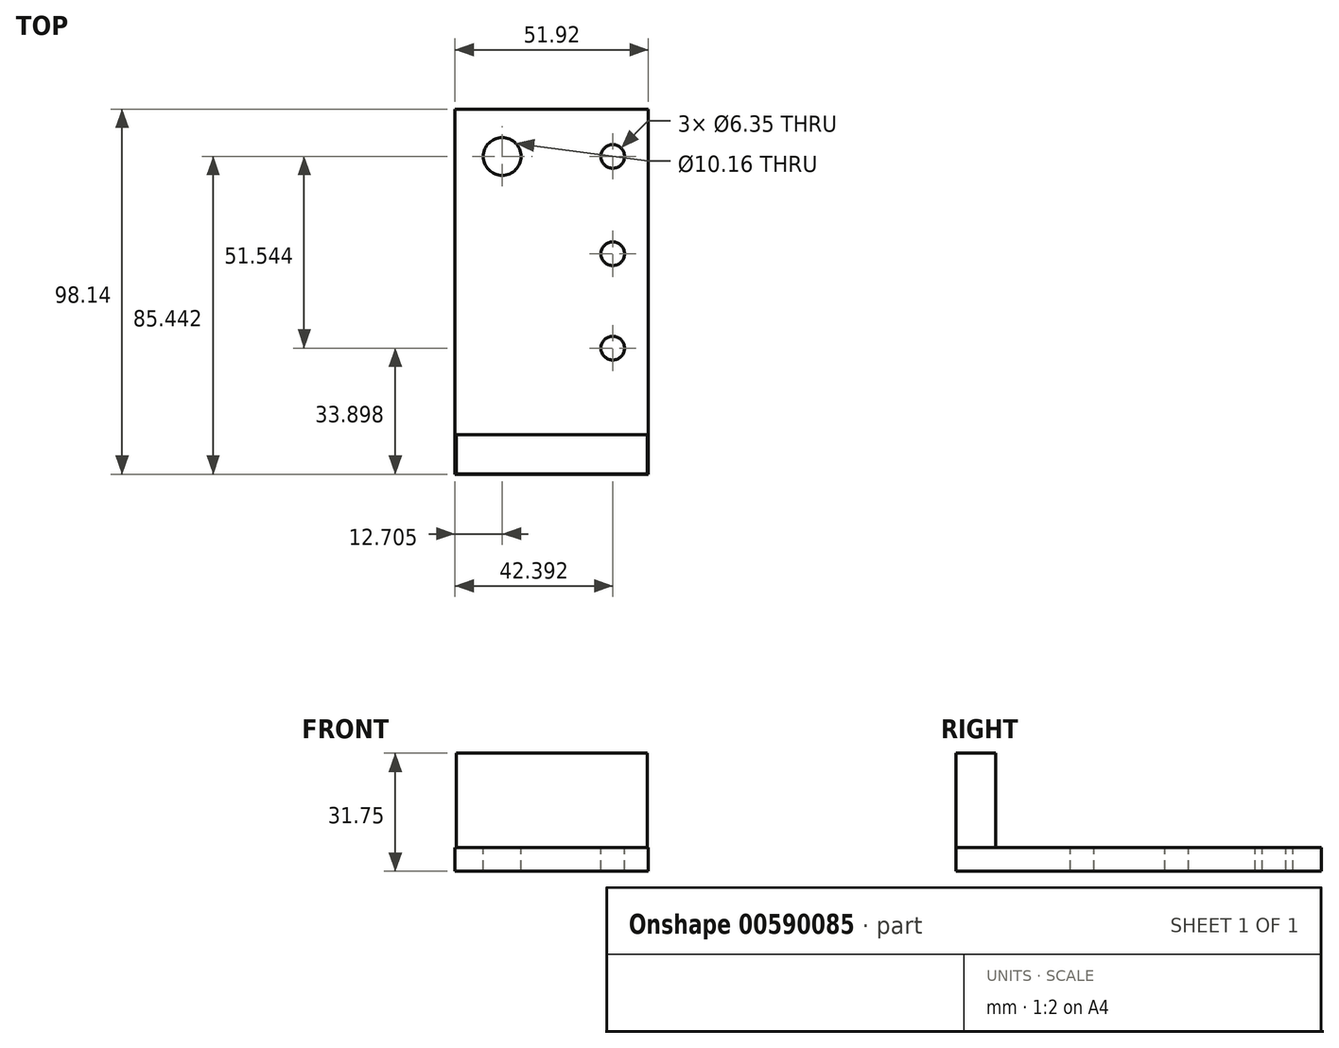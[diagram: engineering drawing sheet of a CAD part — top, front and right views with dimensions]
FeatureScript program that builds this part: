
annotation { "Feature Type Name" : "Feature", "Feature Type Description" : "" }
export const myFeature = defineFeature(function(context is Context, id is Id, definition is map)
    precondition{}
    {
        {
            var Q0;
            Q0=qCreatedBy(makeId("Top.planeOp"),FACE);
            var sketch = newSketch(context, id + "F0", { "sketchPlane" : qUnion([Q0])});
            skLineSegment(sketch, "E0.bottom", {"start": v(-16.24, -40.51) * mm, "end": v(35.68, -40.51) * mm});
            skLineSegment(sketch, "E0.top", {"start": v(-16.24, 57.63) * mm, "end": v(35.68, 57.63) * mm});
            skLineSegment(sketch, "E0.left", {"start": v(-16.24, -40.51) * mm, "end": v(-16.24, 57.63) * mm});
            skLineSegment(sketch, "E0.right", {"start": v(35.68, -40.51) * mm, "end": v(35.68, 57.63) * mm});
            skSolve(sketch);
        }
        {
            var Q0;
            Q0=qCreatedBy(makeId("Top.planeOp"),FACE);
            var sketch = newSketch(context, id + "F1", { "sketchPlane" : qUnion([Q0])});
            skLineSegment(sketch, "E1.bottom", {"start": v(-15.85, -40.5) * mm, "end": v(35.4, -40.5) * mm});
            skLineSegment(sketch, "E1.top", {"start": v(-15.85, -29.94) * mm, "end": v(35.4, -29.94) * mm});
            skLineSegment(sketch, "E1.left", {"start": v(-15.85, -40.5) * mm, "end": v(-15.85, -29.94) * mm});
            skLineSegment(sketch, "E1.right", {"start": v(35.4, -40.5) * mm, "end": v(35.4, -29.94) * mm});
            skSolve(sketch);
        }
        {
            var Q0;
            Q0 = qSketchRegion(id + "F1", true);
            extrude(context, id + "F2", {"entities" : qUnion([Q0]), "depth" : 25.4 * mm, "offsetDistance" : 25.4 * mm});
        }
        {
            var Q0;
            Q0 = qSketchRegion(id + "F0", true);
            extrude(context, id + "F3", {"entities" : qUnion([Q0]), "operationType" : NewBodyOperationType.ADD, "oppositeDirection" : true, "depth" : 6.35 * mm, "offsetDistance" : 25.4 * mm});
        }
        {
            var Q0;
            Q0=makeQuery(id+"F3.opExtrude","CAP_FACE",FACE,{"disambiguationData":[OSD([sQuery(id+"F0.wireOp",EDGE,"E0.bottom"),sQuery(id+"F0.wireOp",EDGE,"E0.top"),sQuery(id+"F0.wireOp",EDGE,"E0.left"),sQuery(id+"F0.wireOp",EDGE,"E0.right")])],"isStart":true});
            var sketch = newSketch(context, id + "F4", { "sketchPlane" : qUnion([Q0])});
            skCircle(sketch, "E2", {"center": v(-3.54, 44.93) * mm, "radius": 5.08 * mm});
            skCircle(sketch, "E3", {"center": v(26.15, 44.93) * mm, "radius": 3.18 * mm});
            skCircle(sketch, "E4", {"center": v(26.15, 18.75) * mm, "radius": 3.18 * mm});
            skCircle(sketch, "E5", {"center": v(26.15, -6.61) * mm, "radius": 3.18 * mm});
            skSolve(sketch);
        }
        {
            var Q0;
            Q0 = qSketchRegion(id + "F4", true);
            extrude(context, id + "F5", {"entities" : qUnion([Q0]), "operationType" : NewBodyOperationType.REMOVE, "oppositeDirection" : true, "depth" : 27.43 * mm, "offsetDistance" : 25.4 * mm});
        }
    });
